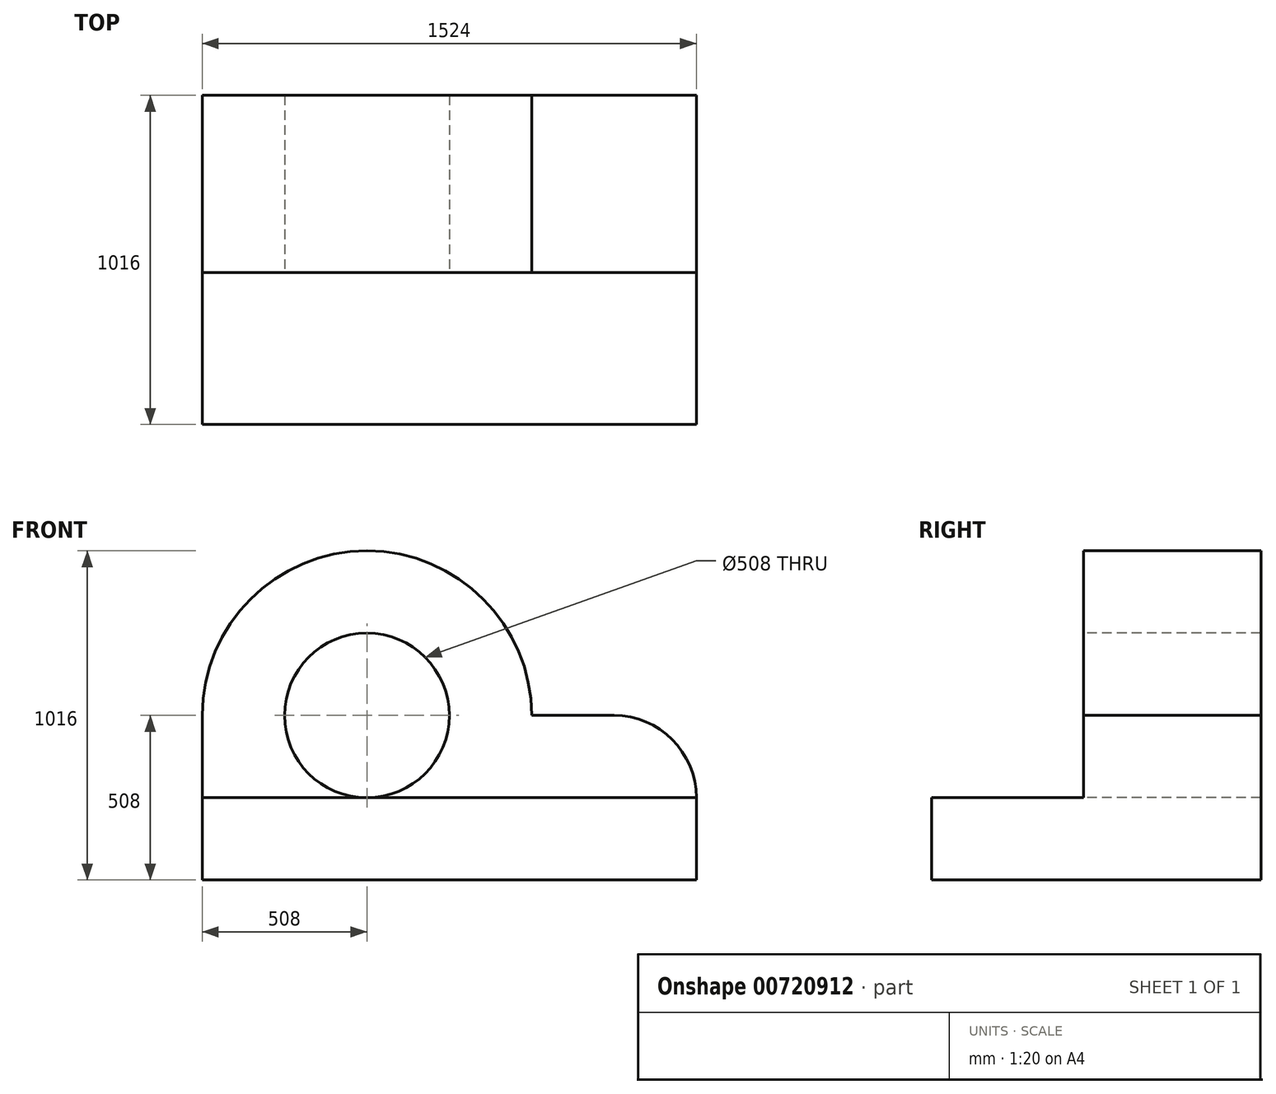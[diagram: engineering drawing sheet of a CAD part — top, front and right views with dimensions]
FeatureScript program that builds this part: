
annotation { "Feature Type Name" : "Feature", "Feature Type Description" : "" }
export const myFeature = defineFeature(function(context is Context, id is Id, definition is map)
    precondition{}
    {
        {
            var Q0;
            Q0=qCreatedBy(makeId("Top.planeOp"),FACE);
            var sketch = newSketch(context, id + "F0", { "sketchPlane" : qUnion([Q0])});
            skLineSegment(sketch, "E0.bottom", {"start": v(0, 0) * mm, "end": v(1524, 0) * mm});
            skLineSegment(sketch, "E0.top", {"start": v(0, -1016) * mm, "end": v(1524, -1016) * mm});
            skLineSegment(sketch, "E0.left", {"start": v(0, 0) * mm, "end": v(0, -1016) * mm});
            skLineSegment(sketch, "E0.right", {"start": v(1524, 0) * mm, "end": v(1524, -1016) * mm});
            skSolve(sketch);
        }
        {
            var Q0;
            Q0=makeQuery(id+"F0.imprint","IMPRINT",FACE,{"disambiguationData":[TD([[makeQuery(id+"F0.imprint","IMPRINT",EDGE,{"derivedFrom":sQuery(id+"F0.wireOp",EDGE,"E0.bottom")}),-1.0]])]});
            extrude(context, id + "F1", {"entities" : qUnion([Q0]), "depth" : 508 * mm, "offsetDistance" : 25.4 * mm});
        }
        {
            var Q0;
            Q0=makeQuery(id+"F1.opExtrude","CAP_FACE",FACE,{"disambiguationData":[OSD([sQuery(id+"F0.wireOp",EDGE,"E0.bottom"),sQuery(id+"F0.wireOp",EDGE,"E0.top"),sQuery(id+"F0.wireOp",EDGE,"E0.left"),sQuery(id+"F0.wireOp",EDGE,"E0.right")])],"isStart":false});
            var sketch = newSketch(context, id + "F2", { "sketchPlane" : qUnion([Q0])});
            skLineSegment(sketch, "E1.bottom", {"start": v(0, 0) * mm, "end": v(1524, 0) * mm});
            skLineSegment(sketch, "E1.top", {"start": v(0, -547.35) * mm, "end": v(1524, -547.35) * mm});
            skLineSegment(sketch, "E1.left", {"start": v(0, 0) * mm, "end": v(0, -547.35) * mm});
            skLineSegment(sketch, "E1.right", {"start": v(1524, 0) * mm, "end": v(1524, -547.35) * mm});
            skSolve(sketch);
        }
        {
            var Q0;
            {var subQ0=sQuery(id+"F2.wireOp",EDGE,"E1.top");Q0=makeQuery(id+"F2.imprint","IMPRINT",FACE,{"disambiguationData":[TD([[makeQuery(id+"F2.imprint","IMPRINT",EDGE,{"derivedFrom":subQ0}),-1.0]])]});}
            extrude(context, id + "F3", {"entities" : qUnion([Q0]), "operationType" : NewBodyOperationType.REMOVE, "oppositeDirection" : true, "depth" : 254 * mm, "offsetDistance" : 25.4 * mm});
        }
        {
            var Q0;
            Q0=makeQuery(id+"F1.opExtrude","CAP_EDGE",EDGE,{"disambiguationData":[OSD([sQuery(id+"F0.wireOp",EDGE,"E0.right")])],"isStart":false});
            fillet(context, id + "F4", {"entities" : qUnion([Q0]), "radius" : 254 * mm, "tangentPropagation" : true, "allowEdgeOverflow" : false});
        }
        {
            var Q0;
            Q0=makeQuery(id+"F1.opExtrude","CAP_FACE",FACE,{"disambiguationData":[OSD([sQuery(id+"F0.wireOp",EDGE,"E0.bottom"),sQuery(id+"F0.wireOp",EDGE,"E0.top"),sQuery(id+"F0.wireOp",EDGE,"E0.left"),sQuery(id+"F0.wireOp",EDGE,"E0.right")])],"isStart":false});
            extrude(context, id + "F5", {"entities" : qUnion([Q0]), "operationType" : NewBodyOperationType.ADD, "depth" : 508 * mm, "offsetDistance" : 25.4 * mm});
        }
        {
            var Q0;
            {var subQ0=sQuery(id+"F2.wireOp",EDGE,"E1.top");Q0=makeQuery(id+"F5.boolean.opBoolean","MERGE",FACE,{"derivedFrom":[makeQuery(id+"F3.boolean.opBoolean","COPY",FACE,{"derivedFrom":makeQuery(id+"F3.opExtrude","SWEPT_FACE",FACE,{"disambiguationData":[OSD([subQ0])]})}),makeQuery(id+"F5.opExtrude","SWEPT_FACE",FACE,{"disambiguationData":[OSD([subQ0])]})]});}
            var sketch = newSketch(context, id + "F6", { "sketchPlane" : qUnion([Q0])});
            skLineSegment(sketch, "E2", {"start": v(0, 508) * mm, "end": v(1016, 508) * mm});
            skLineSegment(sketch, "E3", {"start": v(0, 1016) * mm, "end": v(508, 1016) * mm});
            skArc(sketch, "E4", {"start": v(1016, 508) * mm, "mid": v(508, 1016) * mm, "end": v(0, 508) * mm});
            skLineSegment(sketch, "E5", {"start": v(1016, 508) * mm, "end": v(1270, 508) * mm});
            skSolve(sketch);
        }
        {
            var Q0;
            {var subQ0=sQuery(id+"F6.wireOp",EDGE,"E3");Q0=makeQuery(id+"F6.imprint","IMPRINT",FACE,{"disambiguationData":[TD([[makeQuery(id+"F6.imprint","IMPRINT",EDGE,{"derivedFrom":subQ0}),-1.0]])]});}
            var Q1;
            {var subQ0=sQuery(id+"F6.wireOp",EDGE,"E5");Q1=makeQuery(id+"F6.imprint","IMPRINT",FACE,{"disambiguationData":[TD([[makeQuery(id+"F6.imprint","IMPRINT",EDGE,{"derivedFrom":subQ0}),1.0]])]});}
            extrude(context, id + "F7", {"entities" : qUnion([Q0, Q1]), "operationType" : NewBodyOperationType.REMOVE, "oppositeDirection" : true, "depth" : 1143 * mm, "offsetDistance" : 25.4 * mm});
        }
        {
            var Q0;
            {var subQ0=sQuery(id+"F2.wireOp",EDGE,"E1.top");Q0=makeQuery(id+"F5.boolean.opBoolean","MERGE",FACE,{"derivedFrom":[makeQuery(id+"F3.boolean.opBoolean","COPY",FACE,{"derivedFrom":makeQuery(id+"F3.opExtrude","SWEPT_FACE",FACE,{"disambiguationData":[OSD([subQ0])]})}),makeQuery(id+"F5.opExtrude","SWEPT_FACE",FACE,{"disambiguationData":[OSD([subQ0])]})]});}
            var sketch = newSketch(context, id + "F8", { "sketchPlane" : qUnion([Q0])});
            skCircle(sketch, "E6", {"center": v(508, 508) * mm, "radius": 254 * mm});
            skSolve(sketch);
        }
        {
            var Q0;
            Q0=makeQuery(id+"F8.imprint","IMPRINT",FACE,{"disambiguationData":[TD([[makeQuery(id+"F8.imprint","IMPRINT",EDGE,{"derivedFrom":sQuery(id+"F8.wireOp",EDGE,"E6")}),1.0]])]});
            extrude(context, id + "F9", {"entities" : qUnion([Q0]), "operationType" : NewBodyOperationType.REMOVE, "oppositeDirection" : true, "depth" : 1143 * mm, "offsetDistance" : 25.4 * mm});
        }
    });
